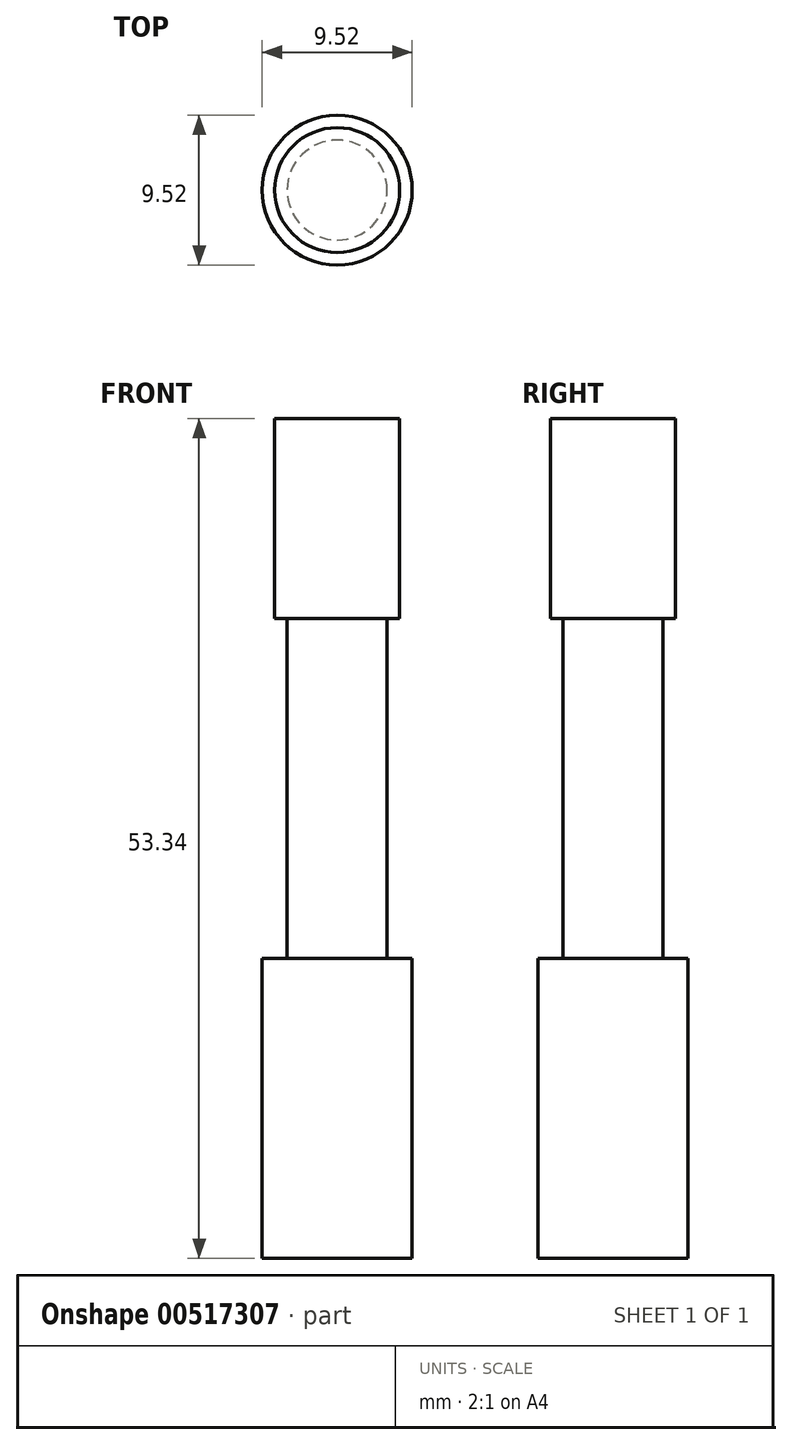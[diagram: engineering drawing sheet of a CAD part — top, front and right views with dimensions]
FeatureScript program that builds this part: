
annotation { "Feature Type Name" : "Feature", "Feature Type Description" : "" }
export const myFeature = defineFeature(function(context is Context, id is Id, definition is map)
    precondition{}
    {
        {
            var Q0;
            Q0=qCreatedBy(makeId("Top.planeOp"),FACE);
            var sketch = newSketch(context, id + "F0", { "sketchPlane" : qUnion([Q0])});
            skCircle(sketch, "E0", {"center": v(0, 0) * mm, "radius": 4.76 * mm});
            skSolve(sketch);
        }
        {
            var Q0;
            Q0=makeQuery(id+"F0.imprint","IMPRINT",FACE,{"disambiguationData":[TD([[makeQuery(id+"F0.imprint","IMPRINT",EDGE,{"derivedFrom":sQuery(id+"F0.wireOp",EDGE,"E0")}),1.0]])]});
            extrude(context, id + "F1", {"entities" : qUnion([Q0]), "depth" : 19.05 * mm, "offsetDistance" : 25.4 * mm});
        }
        {
            var Q0;
            Q0=makeQuery(id+"F1.opExtrude","CAP_FACE",FACE,{"disambiguationData":[OSD([sQuery(id+"F0.wireOp",EDGE,"E0")])],"isStart":false});
            var sketch = newSketch(context, id + "F2", { "sketchPlane" : qUnion([Q0])});
            skCircle(sketch, "E1", {"center": v(0, 0) * mm, "radius": 3.18 * mm});
            skSolve(sketch);
        }
        {
            var Q0;
            Q0 = qSketchRegion(id + "F2", true);
            extrude(context, id + "F3", {"entities" : qUnion([Q0]), "operationType" : NewBodyOperationType.ADD, "depth" : 21.59 * mm, "offsetDistance" : 25.4 * mm});
        }
        {
            var Q0;
            Q0=makeQuery(id+"F3.opExtrude","CAP_FACE",FACE,{"disambiguationData":[OSD([sQuery(id+"F2.wireOp",EDGE,"E1")])],"isStart":false});
            var sketch = newSketch(context, id + "F4", { "sketchPlane" : qUnion([Q0])});
            skCircle(sketch, "E2", {"center": v(0, 0) * mm, "radius": 3.97 * mm});
            skSolve(sketch);
        }
        {
            var Q0;
            Q0 = qSketchRegion(id + "F4", true);
            extrude(context, id + "F5", {"entities" : qUnion([Q0]), "operationType" : NewBodyOperationType.ADD, "depth" : 12.7 * mm, "offsetDistance" : 25.4 * mm});
        }
    });
